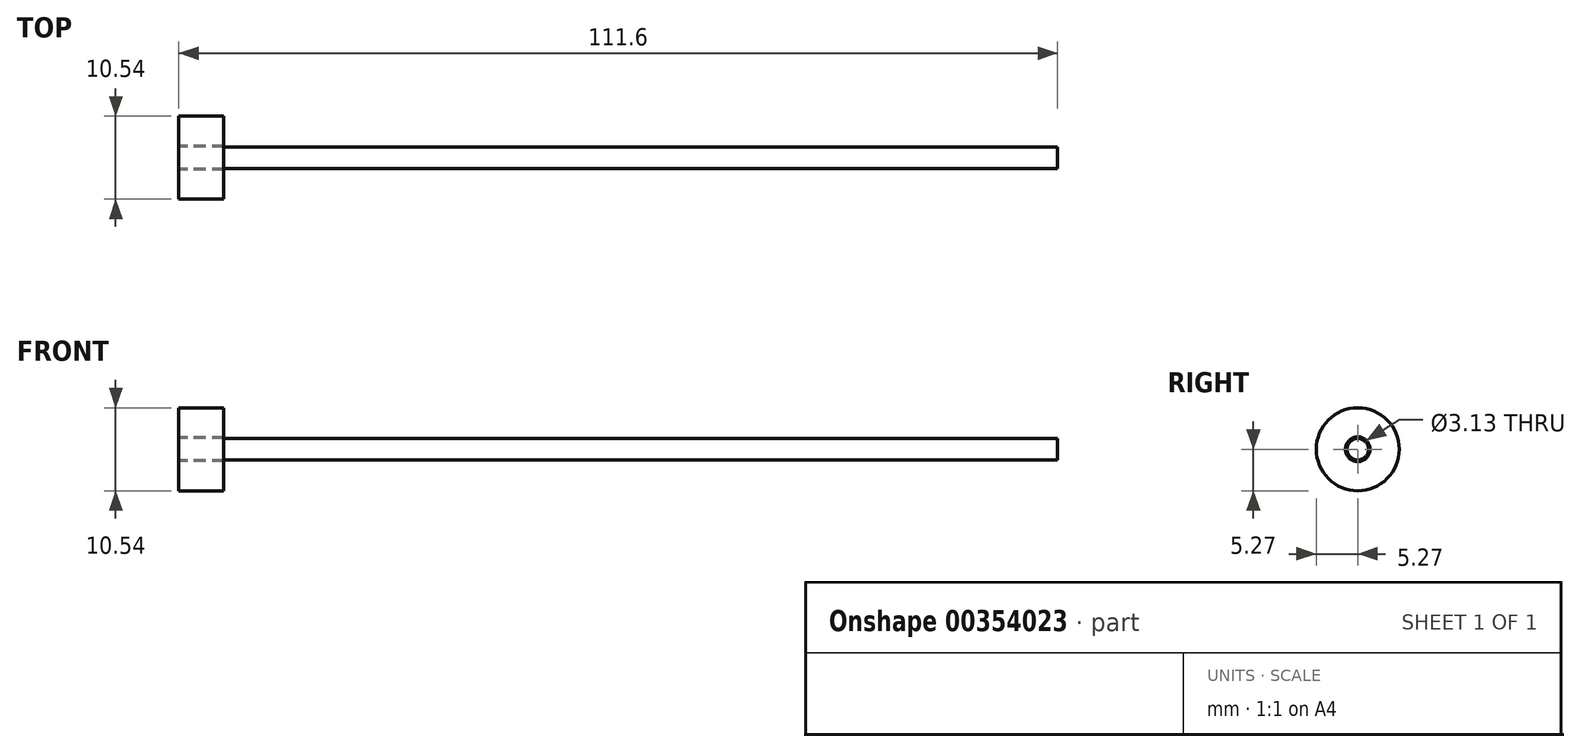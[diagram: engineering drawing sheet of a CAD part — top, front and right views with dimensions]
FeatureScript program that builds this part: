
annotation { "Feature Type Name" : "Feature", "Feature Type Description" : "" }
export const myFeature = defineFeature(function(context is Context, id is Id, definition is map)
    precondition{}
    {
        {
            var Q0;
            Q0=qCreatedBy(makeId("Right.planeOp"),FACE);
            var sketch = newSketch(context, id + "F0", { "sketchPlane" : qUnion([Q0])});
            skCircle(sketch, "E0", {"center": v(0, 0) * mm, "radius": 1.37 * mm});
            skSolve(sketch);
        }
        {
            var Q0;
            Q0 = qSketchRegion(id + "F0", true);
            extrude(context, id + "F1", {"entities" : qUnion([Q0]), "depth" : 111.6 * mm});
        }
        {
            var Q0;
            Q0=qCreatedBy(makeId("Right.planeOp"),FACE);
            var sketch = newSketch(context, id + "F2", { "sketchPlane" : qUnion([Q0])});
            skCircle(sketch, "E1", {"center": v(0, 0) * mm, "radius": 5.27 * mm});
            skCircle(sketch, "E2", {"center": v(0, 0) * mm, "radius": 1.56 * mm});
            skSolve(sketch);
        }
        {
            var Q0;
            Q0 = qSketchRegion(id + "F2", true);
            extrude(context, id + "F3", {"entities" : qUnion([Q0]), "depth" : 5.7 * mm});
        }
    });
